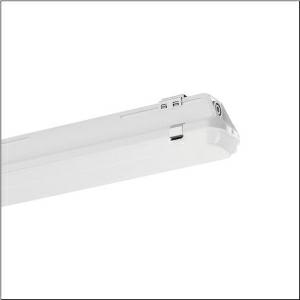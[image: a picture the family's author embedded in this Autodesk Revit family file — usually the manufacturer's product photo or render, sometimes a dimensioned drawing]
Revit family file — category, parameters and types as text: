
# Revit family: monsun_r__21_parking_51fg20dp440bhd_61d3
name_source: partatom
category: Lighting Fixtures
units: mm (PartAtom-declared; Revit-internal decimal feet)

## family parameters
Cut with Voids When Loaded = No
Host = Face
Light Source = No
Part Type = Normal
Room Calculation Point = No
Round Connector Dimension = Use Diameter
Shared = No

## types (1)
- --- (1 x LED, 4810 lm, 37.4 W, 4000K)
    Apparent Load = 37 VA
    CIE Flux Codes = 45 75 93 94 100
    Color Rendering = 80
    Color Temperature = 4000K
    Default Elevation = 1800 mm
    Description = Monsun® 21 parking, damp-proof luminaire, chain hanger, primary optical cover: enclosure, of PC, light emission: direct distribution, primary light characteristic: symmetric, installation type: suspended mounting, surface-mounted, horizontal mounting, vertical mounting, LED, rated luminous flux: 4.810lm, luminous efficacy: 129lm/W, light colour: 840, colour temperature: 4000K, control gear: ECG DALI, with terminal, 5-pole, max. 2.5mm², mains connection: 220..240V, AC, 50/60Hz, rated input power: 37W, housing, of glass-fibre reinforced polyester, uncoated, bright grey, length: 1.590mm, width: 90mm, height: 88mm, clip for enclosure, of stainless steel (V2A), ceiling mounting element, of stainless steel (V2A), chain hanger, of stainless steel (V2A), DALIeco controller, master, sensor HC1, protection rating (complete): IP66, insulation class (complete): insulation class I (protective earthing), certification: CE, ENEC, VDE, UKCA, protection symbol: D, impact resistance: IK08, permissible operating ambient temperature: -20..+35°C, standard: EN 50419, EN 60598-2-1, corresponds to IFS (International Featured Standards) requirements for safety and quality in the food industry, for indoor or canopied outdoor use, no direct snow, no direct sun, no direct rain, packaging unit: 1 piece
    Height = 89 mm
    Lamp = 1 x LED
    Lamp Light Flux = 4810 lm
    Lamp Power = 37.4 W
    Lamp count = 1
    Length = 1590 mm
    Luminous efficacy = 129 lm/W
    Manufacturer = Siteco
    ModVariant = No
    Model = 51FG20DP440BHD
    Mounting Place = Ceiling
    Mounting Type = Pendant
    Number of Poles = 1
    OnlyDefault = Yes
    Power Factor = 1
    Product Name = Monsun® 21 parking
    Product group = damp-proof luminaire | ceiling pendant
    ProductGroupID = 908
    Protection Class = Protection class I
    Protection Degree = IP 66
    RLX_Detail_Level = 1
    RlxData = <blob elided: 91877 chars, md5=a3f68cf6>
    Socket = socket
    Standby Power = 0 W
    System Light Flux = 4810 lm
    System Power = 37 W
    Type Comments = factory setting: luminous flux: 100 % | dim-lin: 254 | 228 mA
    Type Image = l_1006717.jpg
    URL = http://relux.com
    VarID = @adj_124741
    Voltage = 0 V
    Weight = 0.00 kg
    Width = 90 mm

## geometry (parser evidence)
native form markers: Blend x4, Sweep x14
no freeform markers — native parametric forms only
